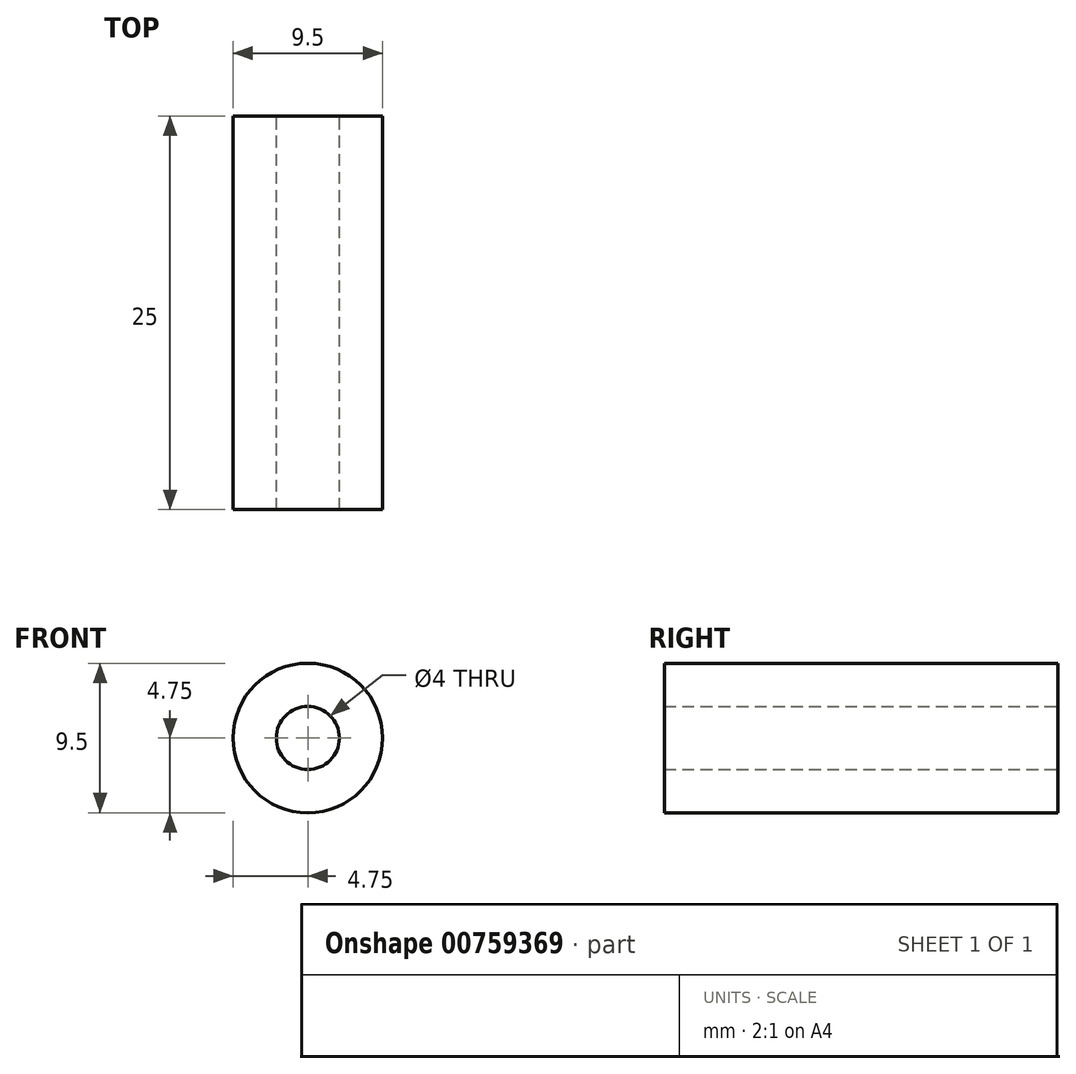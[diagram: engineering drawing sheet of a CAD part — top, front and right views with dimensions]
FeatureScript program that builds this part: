
annotation { "Feature Type Name" : "Feature", "Feature Type Description" : "" }
export const myFeature = defineFeature(function(context is Context, id is Id, definition is map)
    precondition{}
    {
        {
            var Q0;
            Q0=qCreatedBy(makeId("Front.planeOp"),FACE);
            var sketch = newSketch(context, id + "F0", { "sketchPlane" : qUnion([Q0])});
            skCircle(sketch, "E0", {"center": v(0, 0) * mm, "radius": 4.75 * mm});
            skSolve(sketch);
        }
        {
            var Q0;
            Q0=makeQuery(id+"F0.imprint","IMPRINT",FACE,{"disambiguationData":[TD([[makeQuery(id+"F0.imprint","IMPRINT",EDGE,{"derivedFrom":sQuery(id+"F0.wireOp",EDGE,"E0")}),1.0]])]});
            var sketch = newSketch(context, id + "F1", { "sketchPlane" : qUnion([Q0])});
            skCircle(sketch, "E1", {"center": v(0, 0) * mm, "radius": 2 * mm});
            skSolve(sketch);
        }
        {
            var Q0;
            Q0=makeQuery(id+"F1.imprint","IMPRINT",FACE,{"disambiguationData":[TD([[makeQuery(id+"F1.imprint","IMPRINT",EDGE,{"derivedFrom":sQuery(id+"F1.wireOp",EDGE,"E1")}),-1.0]])]});
            extrude(context, id + "F2", {"entities" : qUnion([Q0]), "depth" : 25 * mm, "offsetDistance" : 25 * mm});
        }
    });
